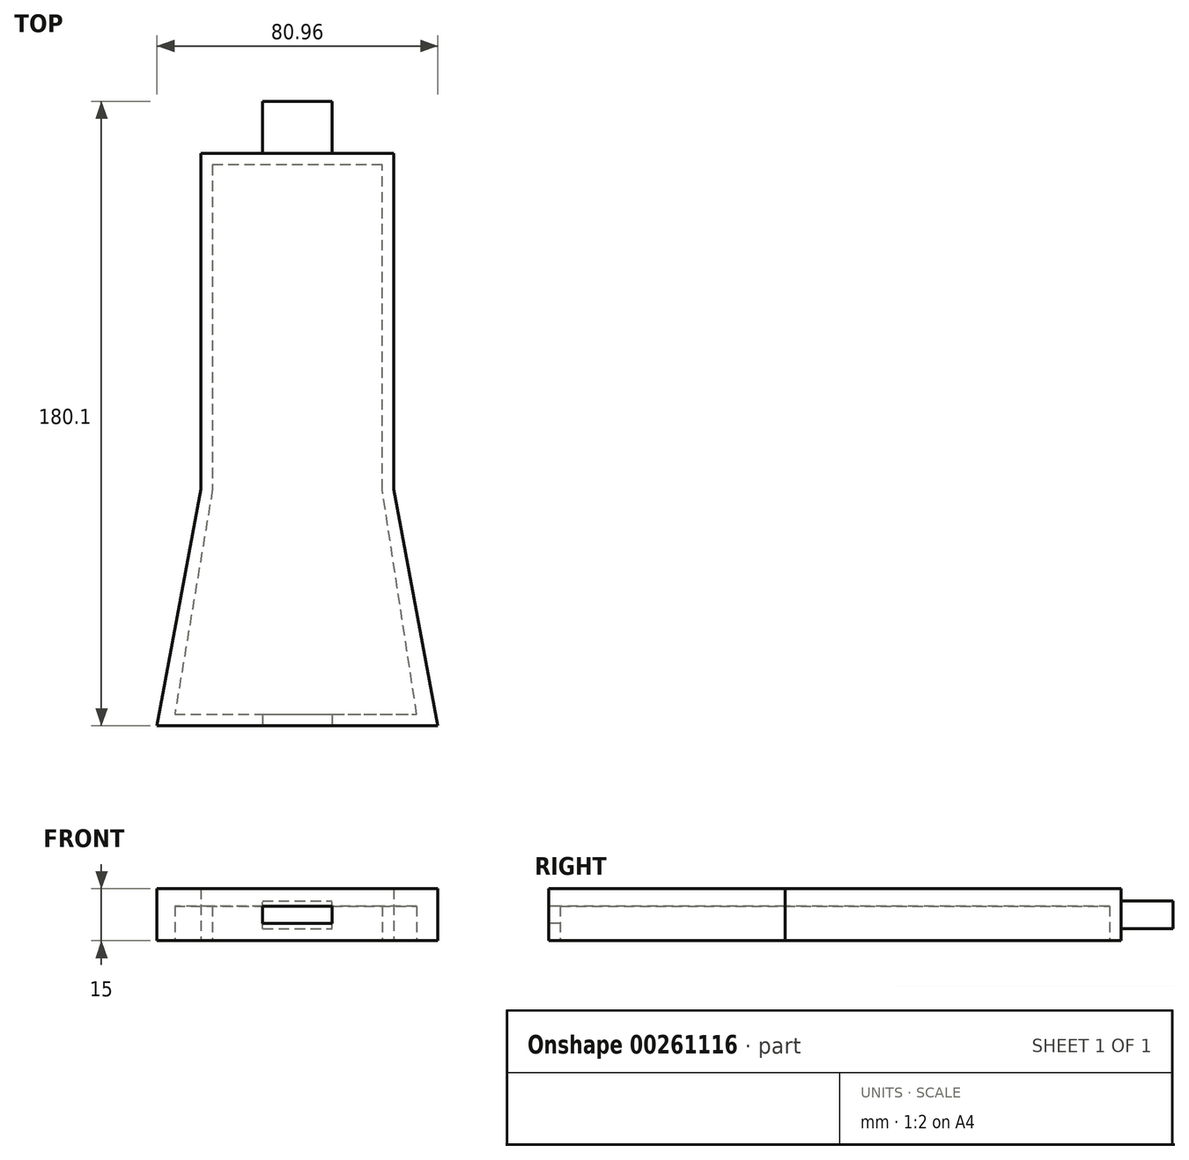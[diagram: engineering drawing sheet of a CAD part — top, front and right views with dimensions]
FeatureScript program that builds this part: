
annotation { "Feature Type Name" : "Feature", "Feature Type Description" : "" }
export const myFeature = defineFeature(function(context is Context, id is Id, definition is map)
    precondition{}
    {
        {
            var Q0;
            Q0=qCreatedBy(makeId("Top.planeOp"),FACE);
            var sketch = newSketch(context, id + "F0", { "sketchPlane" : qUnion([Q0])});
            skLineSegment(sketch, "E0.bottom", {"start": v(27.78, -82.55) * mm, "end": v(-27.78, -82.55) * mm});
            skLineSegment(sketch, "E0.top", {"start": v(27.78, 82.55) * mm, "end": v(-27.78, 82.55) * mm});
            skLineSegment(sketch, "E0.left", {"start": v(27.78, -82.55) * mm, "end": v(27.78, 82.55) * mm});
            skLineSegment(sketch, "E0.right", {"start": v(-27.78, -82.55) * mm, "end": v(-27.78, 82.55) * mm});
            skPoint(sketch, "E0.middle", {"position": v(0, 0) * mm});
            skLineSegment(sketch, "E1.bottom", {"start": v(40.48, -82.55) * mm, "end": v(-40.48, -82.55) * mm});
            skLineSegment(sketch, "E1.top", {"start": v(27.78, -14.29) * mm, "end": v(-27.78, -14.29) * mm});
            skPoint(sketch, "E1.middle", {"position": v(0, -48.42) * mm});
            skLineSegment(sketch, "E2", {"start": v(-27.78, -14.29) * mm, "end": v(-40.48, -82.55) * mm});
            skLineSegment(sketch, "E3", {"start": v(27.78, -14.29) * mm, "end": v(40.48, -82.55) * mm});
            skSolve(sketch);
        }
        {
            var Q0;
            Q0 = qSketchRegion(id + "F0", true);
            extrude(context, id + "F1", {"entities" : qUnion([Q0]), "depth" : 15 * mm});
        }
        {
            var Q0;
            Q0=makeQuery(id+"F1.opExtrude","CAP_FACE",FACE,{"disambiguationData":[OSD([sQuery(id+"F0.wireOp",EDGE,"E0.top"),sQuery(id+"F0.wireOp",EDGE,"E0.left"),sQuery(id+"F0.wireOp",EDGE,"E0.right"),sQuery(id+"F0.wireOp",EDGE,"E1.bottom"),sQuery(id+"F0.wireOp",EDGE,"E2"),sQuery(id+"F0.wireOp",EDGE,"E3")])],"isStart":true});
            var sketch = newSketch(context, id + "F2", { "sketchPlane" : qUnion([Q0])});
            skLineSegment(sketch, "E4", {"start": v(-35.4, 79.25) * mm, "end": v(34.44, 79.25) * mm});
            skLineSegment(sketch, "E5", {"start": v(34.44, 79.25) * mm, "end": v(24.48, 14.4) * mm});
            skLineSegment(sketch, "E6", {"start": v(24.48, 14.4) * mm, "end": v(24.48, -79.25) * mm});
            skLineSegment(sketch, "E7", {"start": v(24.48, -79.25) * mm, "end": v(-24.48, -79.25) * mm});
            skLineSegment(sketch, "E8", {"start": v(-24.48, -79.25) * mm, "end": v(-24.48, 14.29) * mm});
            skLineSegment(sketch, "E9", {"start": v(-24.48, 14.29) * mm, "end": v(-35.4, 79.25) * mm});
            skSolve(sketch);
        }
        {
            var Q0;
            Q0 = qSketchRegion(id + "F2", true);
            extrude(context, id + "F3", {"entities" : qUnion([Q0]), "operationType" : NewBodyOperationType.REMOVE, "oppositeDirection" : true, "depth" : 10 * mm});
        }
        {
            var Q0;
            Q0=makeQuery(id+"F1.opExtrude","SWEPT_FACE",FACE,{"disambiguationData":[OSD([sQuery(id+"F0.wireOp",EDGE,"E1.bottom")])]});
            var sketch = newSketch(context, id + "F4", { "sketchPlane" : qUnion([Q0])});
            skLineSegment(sketch, "E10.bottom", {"start": v(10, 5) * mm, "end": v(-10, 5) * mm});
            skLineSegment(sketch, "E10.top", {"start": v(10, 10) * mm, "end": v(-10, 10) * mm});
            skLineSegment(sketch, "E10.left", {"start": v(10, 5) * mm, "end": v(10, 10) * mm});
            skLineSegment(sketch, "E10.right", {"start": v(-10, 5) * mm, "end": v(-10, 10) * mm});
            skPoint(sketch, "E10.middle", {"position": v(0, 7.5) * mm});
            skSolve(sketch);
        }
        {
            var Q0;
            Q0 = qSketchRegion(id + "F4", true);
            extrude(context, id + "F5", {"entities" : qUnion([Q0]), "operationType" : NewBodyOperationType.REMOVE, "oppositeDirection" : true, "depth" : 25 * mm});
        }
        {
            var Q0;
            Q0=makeQuery(id+"F1.opExtrude","SWEPT_FACE",FACE,{"disambiguationData":[OSD([sQuery(id+"F0.wireOp",EDGE,"E0.top")])]});
            var sketch = newSketch(context, id + "F6", { "sketchPlane" : qUnion([Q0])});
            skLineSegment(sketch, "E11.bottom", {"start": v(10, 3.5) * mm, "end": v(-10, 3.5) * mm});
            skLineSegment(sketch, "E11.top", {"start": v(10, 11.5) * mm, "end": v(-10, 11.5) * mm});
            skLineSegment(sketch, "E11.left", {"start": v(10, 3.5) * mm, "end": v(10, 11.5) * mm});
            skLineSegment(sketch, "E11.right", {"start": v(-10, 3.5) * mm, "end": v(-10, 11.5) * mm});
            skPoint(sketch, "E11.middle", {"position": v(0, 7.5) * mm});
            skSolve(sketch);
        }
        {
            var Q0;
            Q0=makeQuery(id+"F6.imprint","IMPRINT",FACE,{"disambiguationData":[TD([[makeQuery(id+"F6.imprint","IMPRINT",EDGE,{"derivedFrom":sQuery(id+"F6.wireOp",EDGE,"E11.bottom")}),-1.0]])]});
            extrude(context, id + "F7", {"entities" : qUnion([Q0]), "operationType" : NewBodyOperationType.ADD, "depth" : 15 * mm});
        }
    });
